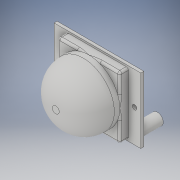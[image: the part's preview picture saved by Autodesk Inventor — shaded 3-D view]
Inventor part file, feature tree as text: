
AUTODESK INVENTOR PART (.ipt)
format: ipt  version: 2017 (Build 210142000, 142)  size: 216,576 bytes
history: native  units: in
note: dims shown in document units (in); Inventor stores cm internally (conversion verified against a paired STEP export)
features: extrude x4, sketch x4, fillet x2, hole x2
ambient origin geometry x8: Origin, YZ Plane, XZ Plane, XY Plane, X Axis, Y Axis, Z Axis, Center Point
bodies: Solid1 (feature_tree)
feature tree (12):
  extrude  "Extrusion1"  Depth=0.95in
  extrude  "Extrusion2"  Depth=0.025in
  extrude  "Extrusion3"  Depth=0.18in
  fillet  "Fillet1"  Radius=0.18in
  fillet  "Fillet2"  Radius=0.125in
  hole  "Hole1"  [1 undecoded]
  hole  "Hole2"  [1 undecoded]
  extrude  "Extrusion4"  Depth=0.345in
  sketch  "Sketch1"  dims[d0=1.26in d1=0.95in]
  sketch  "Sketch2"  dims[d2=0.045in d3=0.0in d4=0.025in]
  sketch  "Sketch3"  dims[d5=0.025in d6=0.18in d7=0.18in d8=0.125in d9=0.0in]
  sketch  "Sketch4"  dims[d10=0.48in d11=0.0in d12=0.4in d13=0.0312in d14=0.09in d15=0.475in d16=0.066in d17=0.75in d18=0.375in d19=0.25in d20=0.5635in d21=1.0in d22=0.8108in d23=0.09in d24=0.475in d25=0.066in d26=0.75in d27=0.375in d28=0.25in d29=0.5635in d30=1.0in d31=0.8108in d32=0.167in d33=0.345in d34=0.0in]
note: 2 required parameter values undecoded (feature->parameter linkage not recoverable at this tier; creation-order binding heuristic only, values carry confidence <= 0.55)
